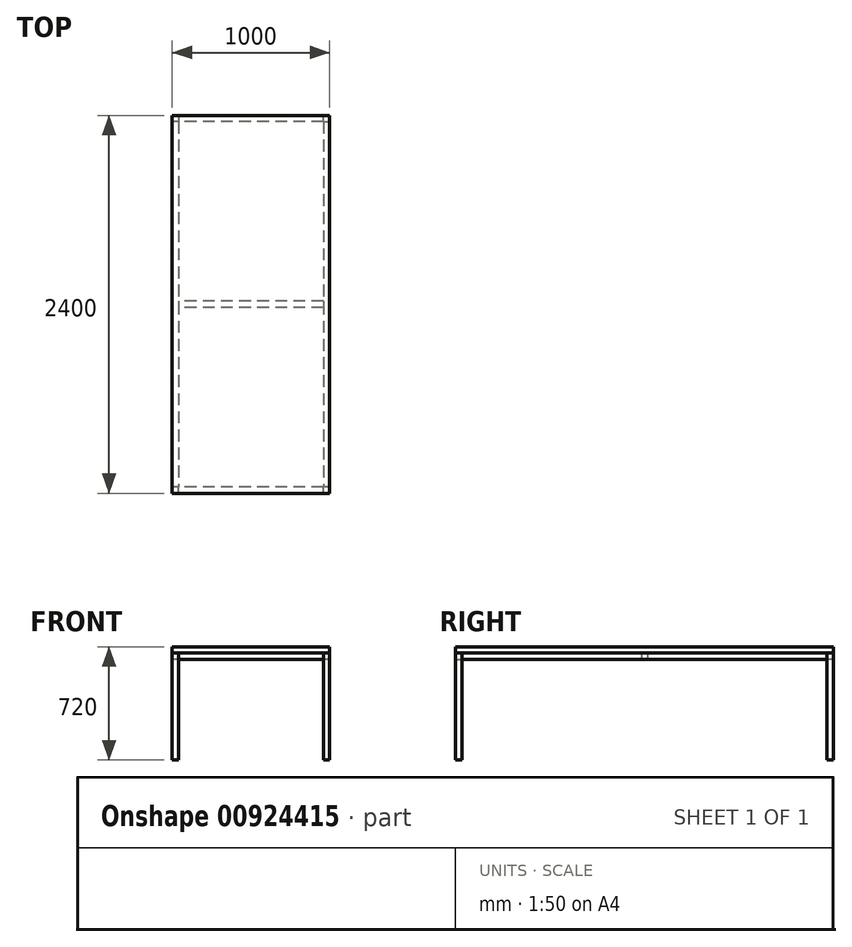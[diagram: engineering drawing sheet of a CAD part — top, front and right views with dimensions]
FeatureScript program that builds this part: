
annotation { "Feature Type Name" : "Feature", "Feature Type Description" : "" }
export const myFeature = defineFeature(function(context is Context, id is Id, definition is map)
    precondition{}
    {
        {
            var Q0;
            Q0=qCreatedBy(makeId("Top.planeOp"),FACE);
            var sketch = newSketch(context, id + "F0", { "sketchPlane" : qUnion([Q0])});
            skLineSegment(sketch, "E0.bottom", {"start": v(0, 0) * mm, "end": v(40, 0) * mm});
            skLineSegment(sketch, "E0.top", {"start": v(0, 40) * mm, "end": v(40, 40) * mm});
            skLineSegment(sketch, "E0.left", {"start": v(0, 0) * mm, "end": v(0, 40) * mm});
            skLineSegment(sketch, "E0.right", {"start": v(40, 0) * mm, "end": v(40, 40) * mm});
            skLineSegment(sketch, "E1.bottom", {"start": v(960, 0) * mm, "end": v(1000, 0) * mm});
            skLineSegment(sketch, "E1.top", {"start": v(960, 40) * mm, "end": v(1000, 40) * mm});
            skLineSegment(sketch, "E1.left", {"start": v(960, 0) * mm, "end": v(960, 40) * mm});
            skLineSegment(sketch, "E1.right", {"start": v(1000, 0) * mm, "end": v(1000, 40) * mm});
            skLineSegment(sketch, "E2.bottom", {"start": v(0, 2360) * mm, "end": v(40, 2360) * mm});
            skLineSegment(sketch, "E2.top", {"start": v(0, 2400) * mm, "end": v(40, 2400) * mm});
            skLineSegment(sketch, "E2.left", {"start": v(0, 2360) * mm, "end": v(0, 2400) * mm});
            skLineSegment(sketch, "E2.right", {"start": v(40, 2360) * mm, "end": v(40, 2400) * mm});
            skLineSegment(sketch, "E3.bottom", {"start": v(960, 2360) * mm, "end": v(1000, 2360) * mm});
            skLineSegment(sketch, "E3.top", {"start": v(960, 2400) * mm, "end": v(1000, 2400) * mm});
            skLineSegment(sketch, "E3.left", {"start": v(960, 2360) * mm, "end": v(960, 2400) * mm});
            skLineSegment(sketch, "E3.right", {"start": v(1000, 2360) * mm, "end": v(1000, 2400) * mm});
            skSolve(sketch);
        }
        {
            var Q0;
            Q0=qSketchRegion(id+"F0",true);
            extrude(context, id + "F1", {"entities" : qUnion([Q0]), "depth" : 680 * mm});
        }
        {
            var Q0;
            Q0=makeQuery(id+"F1.opExtrude","SWEPT_FACE",FACE,{"disambiguationData":[OSD([sQuery(id+"F0.wireOp",EDGE,"E0.top")])]});
            var sketch = newSketch(context, id + "F2", { "sketchPlane" : qUnion([Q0])});
            skLineSegment(sketch, "E4.bottom", {"start": v(-40, 680) * mm, "end": v(0, 680) * mm});
            skLineSegment(sketch, "E4.top", {"start": v(-40, 640) * mm, "end": v(0, 640) * mm});
            skLineSegment(sketch, "E4.left", {"start": v(-40, 680) * mm, "end": v(-40, 640) * mm});
            skLineSegment(sketch, "E4.right", {"start": v(0, 680) * mm, "end": v(0, 640) * mm});
            skSolve(sketch);
        }
        {
            var Q0;
            Q0=makeQuery(id+"F1.opExtrude","SWEPT_FACE",FACE,{"disambiguationData":[OSD([sQuery(id+"F0.wireOp",EDGE,"E1.top")])]});
            var sketch = newSketch(context, id + "F3", { "sketchPlane" : qUnion([Q0])});
            skLineSegment(sketch, "E5.bottom", {"start": v(-1000, 680) * mm, "end": v(-960, 680) * mm});
            skLineSegment(sketch, "E5.top", {"start": v(-1000, 640) * mm, "end": v(-960, 640) * mm});
            skLineSegment(sketch, "E5.left", {"start": v(-1000, 680) * mm, "end": v(-1000, 640) * mm});
            skLineSegment(sketch, "E5.right", {"start": v(-960, 680) * mm, "end": v(-960, 640) * mm});
            skSolve(sketch);
        }
        {
            var Q0;
            Q0=makeQuery(id+"F2.imprint","IMPRINT",FACE,{"disambiguationData":[TD([[makeQuery(id+"F2.imprint","IMPRINT",EDGE,{"derivedFrom":sQuery(id+"F2.wireOp",EDGE,"E4.bottom")}),1.0]])]});
            var Q1;
            Q1=makeQuery(id+"F3.imprint","IMPRINT",FACE,{"disambiguationData":[TD([[makeQuery(id+"F3.imprint","IMPRINT",EDGE,{"derivedFrom":sQuery(id+"F3.wireOp",EDGE,"E5.bottom")}),1.0]])]});
            extrude(context, id + "F4", {"entities" : qUnion([Q0, Q1]), "depth" : (2400 - (2 * 40)) * mm});
        }
        {
            var Q0;
            Q0=makeQuery(id+"F1.opExtrude","SWEPT_FACE",FACE,{"disambiguationData":[OSD([sQuery(id+"F0.wireOp",EDGE,"E0.right")])]});
            var sketch = newSketch(context, id + "F5", { "sketchPlane" : qUnion([Q0])});
            skLineSegment(sketch, "E6.bottom", {"start": v(0, 680) * mm, "end": v(40, 680) * mm});
            skLineSegment(sketch, "E6.top", {"start": v(0, 640) * mm, "end": v(40, 640) * mm});
            skLineSegment(sketch, "E6.left", {"start": v(0, 680) * mm, "end": v(0, 640) * mm});
            skLineSegment(sketch, "E6.right", {"start": v(40, 680) * mm, "end": v(40, 640) * mm});
            skSolve(sketch);
        }
        {
            var Q0;
            Q0=makeQuery(id+"F4.opExtrude","SWEPT_FACE",FACE,{"disambiguationData":[OSD([sQuery(id+"F2.wireOp",EDGE,"E4.left")])]});
            var sketch = newSketch(context, id + "F6", { "sketchPlane" : qUnion([Q0])});
            skLineSegment(sketch, "E7.bottom", {"start": v(1220, 680) * mm, "end": v(1180, 680) * mm});
            skLineSegment(sketch, "E7.top", {"start": v(1220, 640) * mm, "end": v(1180, 640) * mm});
            skLineSegment(sketch, "E7.left", {"start": v(1220, 680) * mm, "end": v(1220, 640) * mm});
            skLineSegment(sketch, "E7.right", {"start": v(1180, 680) * mm, "end": v(1180, 640) * mm});
            skPoint(sketch, "E7.middle", {"position": v(1200, 660) * mm});
            skPoint(sketch, "E7.middle.positionSnap0", {"position": v(1200, 640) * mm});
            skPoint(sketch, "E7.middle.positionSnap1", {"position": v(40, 660) * mm});
            skPoint(sketch, "E7.centerSnap0", {"position": v(1200, 640) * mm});
            skPoint(sketch, "E7.centerSnap1", {"position": v(40, 660) * mm});
            skSolve(sketch);
        }
        {
            var Q0;
            Q0=makeQuery(id+"F1.opExtrude","SWEPT_FACE",FACE,{"disambiguationData":[OSD([sQuery(id+"F0.wireOp",EDGE,"E2.right")])]});
            var sketch = newSketch(context, id + "F7", { "sketchPlane" : qUnion([Q0])});
            skLineSegment(sketch, "E8.bottom", {"start": v(2400, 680) * mm, "end": v(2360, 680) * mm});
            skLineSegment(sketch, "E8.top", {"start": v(2400, 640) * mm, "end": v(2360, 640) * mm});
            skLineSegment(sketch, "E8.left", {"start": v(2400, 680) * mm, "end": v(2400, 640) * mm});
            skLineSegment(sketch, "E8.right", {"start": v(2360, 680) * mm, "end": v(2360, 640) * mm});
            skSolve(sketch);
        }
        {
            var Q0;
            Q0=qSketchRegion(id+"F5",true);
            var Q1;
            Q1=qSketchRegion(id+"F6",true);
            var Q2;
            Q2=qSketchRegion(id+"F7",true);
            extrude(context, id + "F8", {"entities" : qUnion([Q0, Q1, Q2]), "depth" : (1000 - (2 * 40)) * mm});
        }
        {
            var Q0;
            Q0=qCreatedBy(makeId("Front.planeOp"),FACE);
            var sketch = newSketch(context, id + "F9", { "sketchPlane" : qUnion([Q0])});
            skLineSegment(sketch, "E9.bottom", {"start": v(0, 680) * mm, "end": v(1000, 680) * mm});
            skLineSegment(sketch, "E9.top", {"start": v(0, 720) * mm, "end": v(1000, 720) * mm});
            skLineSegment(sketch, "E9.left", {"start": v(0, 680) * mm, "end": v(0, 720) * mm});
            skLineSegment(sketch, "E9.right", {"start": v(1000, 680) * mm, "end": v(1000, 720) * mm});
            skSolve(sketch);
        }
        {
            var Q0;
            Q0=makeQuery(id+"F9.imprint","IMPRINT",FACE,{"disambiguationData":[TD([[makeQuery(id+"F9.imprint","IMPRINT",EDGE,{"derivedFrom":sQuery(id+"F9.wireOp",EDGE,"E9.bottom")}),1.0]])]});
            extrude(context, id + "F10", {"entities" : qUnion([Q0]), "oppositeDirection" : true, "depth" : 2400 * mm});
        }
    });
